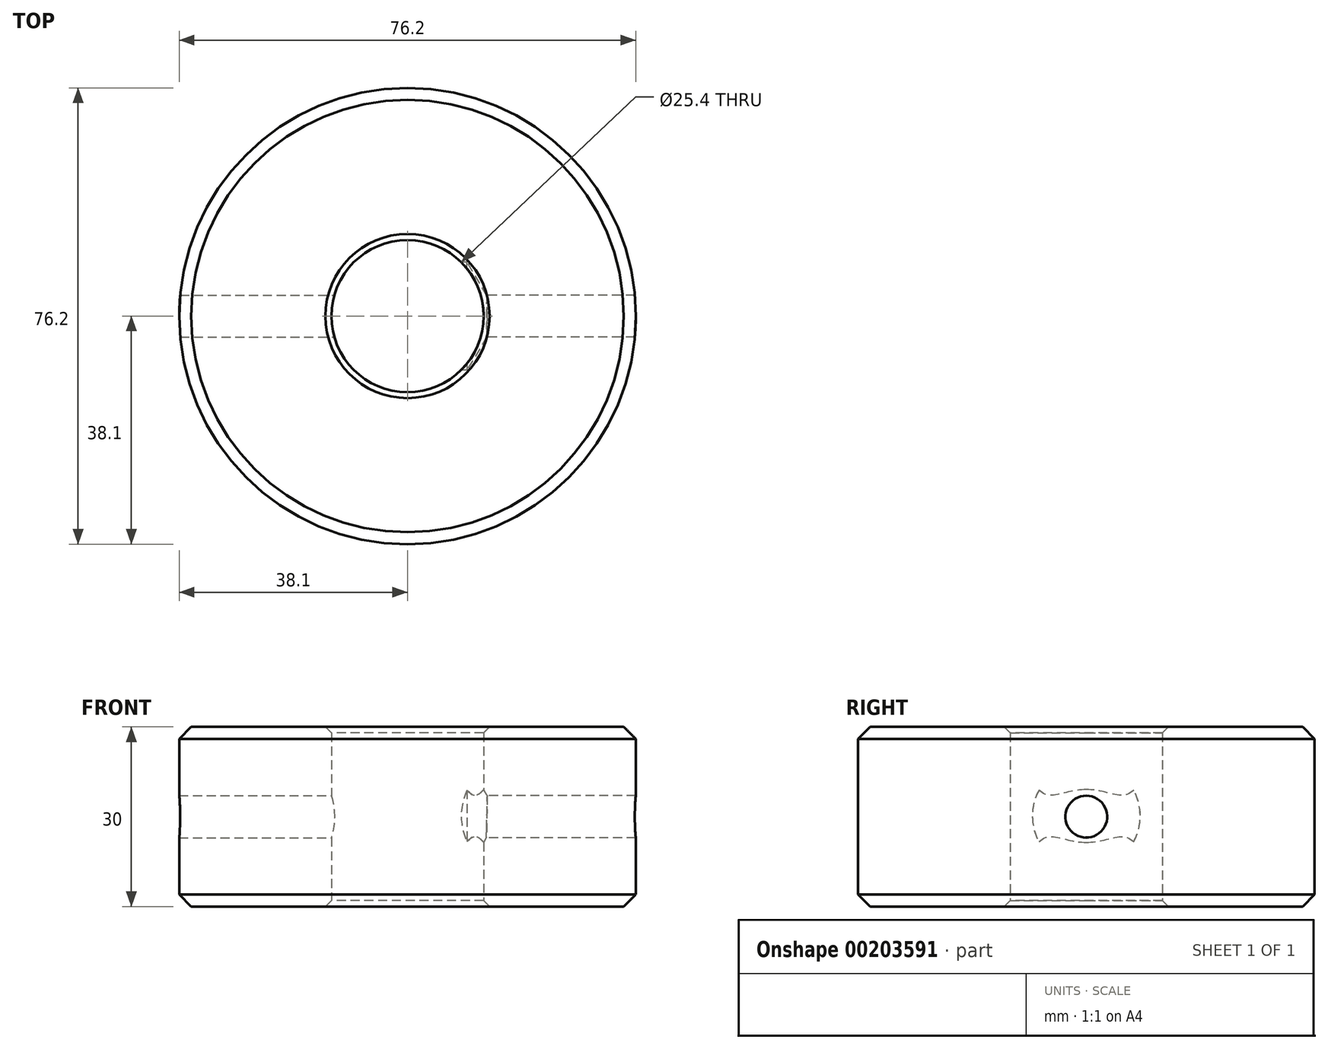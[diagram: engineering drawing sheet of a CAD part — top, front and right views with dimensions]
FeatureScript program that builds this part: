
annotation { "Feature Type Name" : "Feature", "Feature Type Description" : "" }
export const myFeature = defineFeature(function(context is Context, id is Id, definition is map)
    precondition{}
    {
        {
            var Q0;
            Q0=qCreatedBy(makeId("Top.planeOp"),FACE);
            var sketch = newSketch(context, id + "F0", { "sketchPlane" : qUnion([Q0])});
            skCircle(sketch, "E0", {"center": v(0, 0) * mm, "radius": 38.1 * mm});
            skCircle(sketch, "E1", {"center": v(0, 0) * mm, "radius": 12.7 * mm});
            skSolve(sketch);
        }
        {
            var Q0;
            Q0 = qSketchRegion(id + "F0", true);
            extrude(context, id + "F1", {"entities" : qUnion([Q0]), "depth" : 30 * mm});
        }
        {
            var Q0;
            Q0=makeQuery(id+"F1.opExtrude","CAP_EDGE",EDGE,{"disambiguationData":[OSD([sQuery(id+"F0.wireOp",EDGE,"E0")])],"isStart":false});
            var Q1;
            Q1=makeQuery(id+"F1.opExtrude","CAP_EDGE",EDGE,{"disambiguationData":[OSD([sQuery(id+"F0.wireOp",EDGE,"E0")])],"isStart":true});
            chamfer(context, id + "F2", {"entities" : qUnion([Q0, Q1]), "width" : 2 * mm, "tangentPropagation" : true});
        }
        {
            var Q0;
            Q0=qCreatedBy(makeId("Right.planeOp"),FACE);
            var sketch = newSketch(context, id + "F3", { "sketchPlane" : qUnion([Q0])});
            skPoint(sketch, "E2", {"position": v(0, 15) * mm});
            skSolve(sketch);
        }
        {
            var Q0;
            Q0=sQuery(id+"F3.wireOp",VERTEX,"E2");
            var Q1;
            Q1=makeQuery(id+"F1.opExtrude","SWEPT_BODY",BODY,{"disambiguationData":[OSD([sQuery(id+"F0.wireOp",EDGE,"E0"),sQuery(id+"F0.wireOp",EDGE,"E1")])]});
            hole(context, id + "F4", {"style" : HoleStyle.SIMPLE, "endStyle" : HoleEndStyle.THROUGH, "oppositeDirection" : true, "standardTappedOrClearance" : lookupTablePath({ "standard" : "ISO", "engagement" : "75%", "pitch" : "1 mm", "size" : "M8", "type" : "Tapped" }), "standardBlindInLast" : lookupTablePath({ "standard" : "ISO", "engagement" : "75%", "pitch" : "1 mm", "size" : "M8", "type" : "Tapped" }), "holeDiameter" : 7 * mm, "startFromSketch" : true, "locations" : qUnion([Q0]), "scope" : qUnion([Q1]), "isTappedThrough" : true, "majorDiameter" : 8 * mm, "showTappedDepth" : true});
        }
        {
            var Q0;
            Q0=sQuery(id+"F3.wireOp",VERTEX,"E2");
            var Q1;
            Q1=makeQuery(id+"F1.opExtrude","SWEPT_BODY",BODY,{"disambiguationData":[OSD([sQuery(id+"F0.wireOp",EDGE,"E0"),sQuery(id+"F0.wireOp",EDGE,"E1")])]});
            hole(context, id + "F5", {"style" : HoleStyle.SIMPLE, "endStyle" : HoleEndStyle.THROUGH, "standardTappedOrClearance" : lookupTablePath({ "standard" : "ISO", "engagement" : "75%", "pitch" : "1 mm", "size" : "M8", "type" : "Tapped" }), "standardBlindInLast" : lookupTablePath({ "standard" : "ISO", "engagement" : "75%", "pitch" : "1 mm", "size" : "M8", "type" : "Tapped" }), "holeDiameter" : 7 * mm, "startFromSketch" : true, "locations" : qUnion([Q0]), "scope" : qUnion([Q1]), "isTappedThrough" : true, "majorDiameter" : 8 * mm, "showTappedDepth" : true});
        }
        {
            var Q0;
            Q0=qCreatedBy(makeId("Right.planeOp"),FACE);
            cPlane(context, id + "F6", {"entities" : qUnion([Q0]), "cplaneType" : CPlaneType.OFFSET, "offset" : 3 / 50.8 * mm, "oppositeDirection" : true, "width" : 150 * mm, "height" : 150 * mm});
        }
        {
            var Q0;
            Q0=qCreatedBy(id+"F6.planeOp",FACE);
            var sketch = newSketch(context, id + "F7", { "sketchPlane" : qUnion([Q0])});
            skPoint(sketch, "E3", {"position": v(0, 15.12) * mm});
            skSolve(sketch);
        }
        {
            var Q0;
            Q0=sQuery(id+"F7.wireOp",VERTEX,"E3");
            var Q1;
            Q1=makeQuery(id+"F1.opExtrude","SWEPT_BODY",BODY,{"disambiguationData":[OSD([sQuery(id+"F0.wireOp",EDGE,"E0"),sQuery(id+"F0.wireOp",EDGE,"E1")])]});
            hole(context, id + "F8", {"style" : HoleStyle.C_BORE, "endStyle" : HoleEndStyle.BLIND, "oppositeDirection" : true, "holeDiameter" : 18 * mm, "cBoreDiameter" : 25 * mm, "cBoreDepth" : 2 * mm, "holeDepth" : 10 * mm, "startFromSketch" : true, "locations" : qUnion([Q0]), "scope" : qUnion([Q1])});
        }
        {
            var Q0;
            Q0=makeQuery(id+"F1.opExtrude","CAP_EDGE",EDGE,{"disambiguationData":[OSD([sQuery(id+"F0.wireOp",EDGE,"E1")])],"isStart":true});
            var Q1;
            Q1=makeQuery(id+"F1.opExtrude","CAP_EDGE",EDGE,{"disambiguationData":[OSD([sQuery(id+"F0.wireOp",EDGE,"E1")])],"isStart":false});
            chamfer(context, id + "F9", {"entities" : qUnion([Q0, Q1]), "width" : 1 * mm, "tangentPropagation" : true});
        }
    });
